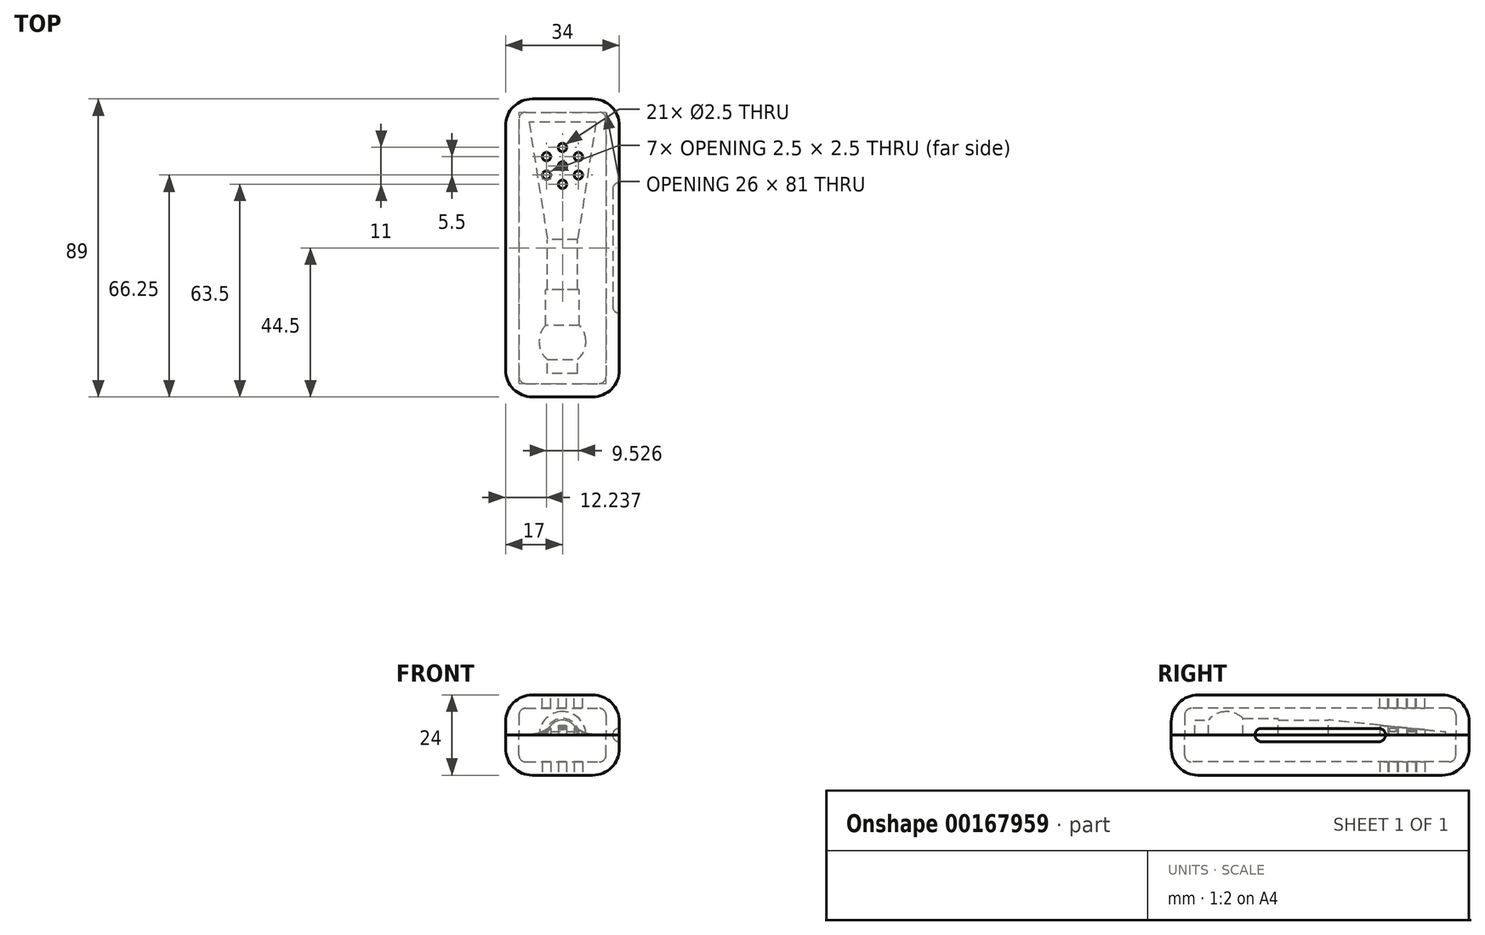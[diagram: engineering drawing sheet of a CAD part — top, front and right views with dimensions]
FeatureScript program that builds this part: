
annotation { "Feature Type Name" : "Feature", "Feature Type Description" : "" }
export const myFeature = defineFeature(function(context is Context, id is Id, definition is map)
    precondition{}
    {
        {
            var Q0;
            Q0=qCreatedBy(makeId("Front.planeOp"),FACE);
            cPlane(context, id + "F0", {"entities" : qUnion([Q0]), "cplaneType" : CPlaneType.OFFSET, "offset" : 35 * mm, "width" : 150 * mm, "height" : 150 * mm});
        }
        {
            var Q0;
            Q0=qCreatedBy(id+"F0.planeOp",FACE);
            var sketch = newSketch(context, id + "F1", { "sketchPlane" : qUnion([Q0])});
            skCircle(sketch, "E0", {"center": v(0, 0) * mm, "radius": 4.5 * mm});
            skSolve(sketch);
        }
        {
            var Q0;
            Q0=qCreatedBy(makeId("Front.planeOp"),FACE);
            var sketch = newSketch(context, id + "F2", { "sketchPlane" : qUnion([Q0])});
            skArc(sketch, "E1", {"start": v(10, 0) * mm, "mid": v(0, 1) * mm, "end": v(-10, 0) * mm});
            skLineSegment(sketch, "E2", {"start": v(-17.72, 1) * mm, "end": v(25.21, 1) * mm, "construction": true});
            skArc(sketch, "E3.MirrorCS", {"start": v(10, 0) * mm, "mid": v(0, -1) * mm, "end": v(-10, 0) * mm});
            skSolve(sketch);
        }
        {
            var Q0;
            Q0=makeQuery(id+"F1.imprint","IMPRINT",FACE,{"disambiguationData":[TD([[makeQuery(id+"F1.imprint","IMPRINT",EDGE,{"derivedFrom":sQuery(id+"F1.wireOp",EDGE,"E0")}),1.0]])]});
            extrude(context, id + "F3", {"entities" : qUnion([Q0]), "depth" : 40 * mm});
        }
        {
            var Q1;
            Q1=makeQuery(id+"F2.imprint","IMPRINT",FACE,{"disambiguationData":[TD([[makeQuery(id+"F2.imprint","IMPRINT",EDGE,{"derivedFrom":sQuery(id+"F2.wireOp",EDGE,"E1")}),1.0]])]});
            var Q2;
            Q2=makeQuery(id+"F1.imprint","IMPRINT",FACE,{"disambiguationData":[TD([[makeQuery(id+"F1.imprint","IMPRINT",EDGE,{"derivedFrom":sQuery(id+"F1.wireOp",EDGE,"E0")}),1.0]])]});
            loft(context, id + "F4", {"operationType" : NewBodyOperationType.ADD, "sheetProfilesArray" : [{ "sheetProfileEntities" : qUnion([Q1]) }, { "sheetProfileEntities" : qUnion([Q2]) }]});
        }
        {
            var Q0;
            Q0=makeQuery(id+"F3.opExtrude","CAP_FACE",FACE,{"disambiguationData":[OSD([sQuery(id+"F1.wireOp",EDGE,"E0")])],"isStart":false});
            cPlane(context, id + "F5", {"entities" : qUnion([Q0]), "cplaneType" : CPlaneType.OFFSET, "offset" : 9.5 * mm, "oppositeDirection" : true, "width" : 150 * mm, "height" : 150 * mm});
        }
        {
            var Q0;
            Q0=qCreatedBy(id+"F5.planeOp",FACE);
            var sketch = newSketch(context, id + "F6", { "sketchPlane" : qUnion([Q0])});
            skArc(sketch, "E4", {"start": v(0, 7) * mm, "mid": v(-7, 0) * mm, "end": v(0, -7) * mm});
            skLineSegment(sketch, "E5", {"start": v(0, 7) * mm, "end": v(0, -7) * mm});
            skSolve(sketch);
        }
        {
            var Q0;
            Q0=makeQuery(id+"F6.imprint","IMPRINT",FACE,{"disambiguationData":[TD([[makeQuery(id+"F6.imprint","IMPRINT",EDGE,{"derivedFrom":sQuery(id+"F6.wireOp",EDGE,"E4")}),1.0]])]});
            var Q1;
            Q1=sQuery(id+"F6.wireOp",EDGE,"E5");
            revolve(context, id + "F7", {"operationType" : NewBodyOperationType.ADD, "entities" : qUnion([Q0]), "axis" : qUnion([Q1]), "revolveType" : RevolveType.FULL});
        }
        {
            var Q0;
            Q0=makeQuery(id+"F3.opExtrude","CAP_FACE",FACE,{"disambiguationData":[OSD([sQuery(id+"F1.wireOp",EDGE,"E0")])],"isStart":false});
            cPlane(context, id + "F8", {"entities" : qUnion([Q0]), "cplaneType" : CPlaneType.OFFSET, "offset" : 25 * mm, "oppositeDirection" : true, "width" : 150 * mm, "height" : 150 * mm});
        }
        {
            var Q0;
            Q0=qCreatedBy(id+"F8.planeOp",FACE);
            var sketch = newSketch(context, id + "F9", { "sketchPlane" : qUnion([Q0])});
            skCircle(sketch, "E6", {"center": v(0, 0) * mm, "radius": 5 * mm});
            skSolve(sketch);
        }
        {
            var Q0;
            Q0=makeQuery(id+"F9.imprint","IMPRINT",FACE,{"disambiguationData":[TD([[makeQuery(id+"F9.imprint","IMPRINT",EDGE,{"derivedFrom":sQuery(id+"F9.wireOp",EDGE,"E6")}),1.0]])]});
            extrude(context, id + "F10", {"entities" : qUnion([Q0]), "operationType" : NewBodyOperationType.ADD, "endBound" : BoundingType.UP_TO_NEXT, "depth" : 25 * mm});
        }
        {
            assignVariable(context, id + "F11", {"name" : "wood", "anyValue" : 4 * mm});
        }
        {
            assignVariable(context, id + "F12", {"name" : "inner_corner", "anyValue" : 2 * mm});
        }
        {
            assignVariable(context, id + "F13", {"name" : "outer_corner", "anyValue" : 8 * mm});
        }
        {
            assignVariable(context, id + "F14", {"name" : "box_thickness", "anyValue" : 12 * mm});
        }
        {
            var Q0;
            Q0=qCreatedBy(makeId("Top.planeOp"),FACE);
            var sketch = newSketch(context, id + "F15", { "sketchPlane" : qUnion([Q0])});
            skLineSegment(sketch, "E7", {"start": v(31.86, 0) * mm, "end": v(31.86, -37.5) * mm, "construction": true});
            skLineSegment(sketch, "E8", {"start": v(31.86, -37.5) * mm, "end": v(31.86, -75) * mm, "construction": true});
            skLineSegment(sketch, "E9", {"start": v(0, 0) * mm, "end": v(31.86, 0) * mm, "construction": true});
            skLineSegment(sketch, "E10", {"start": v(31.86, -75) * mm, "end": v(-31.65, -75) * mm, "construction": true});
            skLineSegment(sketch, "E11.bottom", {"start": v(17, -82) * mm, "end": v(-17, -82) * mm});
            skLineSegment(sketch, "E11.top", {"start": v(17, 7) * mm, "end": v(-17, 7) * mm});
            skLineSegment(sketch, "E11.left", {"start": v(17, -82) * mm, "end": v(17, 7) * mm});
            skLineSegment(sketch, "E11.right", {"start": v(-17, -82) * mm, "end": v(-17, 7) * mm});
            skPoint(sketch, "E11.middle", {"position": v(0, -37.5) * mm});
            skLineSegment(sketch, "E12", {"start": v(31.86, -37.5) * mm, "end": v(-50.29, -37.5) * mm, "construction": true});
            skPoint(sketch, "E13", {"position": v(-9.21, -37.5) * mm});
            skSolve(sketch);
        }
        {
            var Q0;
            Q0=makeQuery(id+"F15.imprint","IMPRINT",FACE,{"disambiguationData":[TD([[makeQuery(id+"F15.imprint","IMPRINT",EDGE,{"derivedFrom":sQuery(id+"F15.wireOp",EDGE,"E11.bottom")}),-1.0]])]});
            extrude(context, id + "F16", {"entities" : qUnion([Q0]), "oppositeDirection" : true, "depth" : getVariable(context, 'box_thickness')});
        }
        {
            var Q0;
            Q0=makeQuery(id+"F16.opExtrude","CAP_FACE",FACE,{"disambiguationData":[OSD([sQuery(id+"F15.wireOp",EDGE,"E11.bottom"),sQuery(id+"F15.wireOp",EDGE,"E11.top"),sQuery(id+"F15.wireOp",EDGE,"E11.left"),sQuery(id+"F15.wireOp",EDGE,"E11.right")])],"isStart":true});
            var sketch = newSketch(context, id + "F17", { "sketchPlane" : qUnion([Q0])});
            skLineSegment(sketch, "E14.bottom", {"start": v(-13, 3) * mm, "end": v(13, 3) * mm});
            skLineSegment(sketch, "E14.top", {"start": v(-13, -78) * mm, "end": v(13, -78) * mm});
            skLineSegment(sketch, "E14.left", {"start": v(-13, 3) * mm, "end": v(-13, -78) * mm});
            skLineSegment(sketch, "E14.right", {"start": v(13, 3) * mm, "end": v(13, -78) * mm});
            skPoint(sketch, "E15.visualSharp", {"position": v(-13, 3) * mm});
            skPoint(sketch, "E16.visualSharp", {"position": v(13, 3) * mm});
            skPoint(sketch, "E17.visualSharp", {"position": v(13, -78) * mm});
            skPoint(sketch, "E18.visualSharp", {"position": v(-13, -78) * mm});
            skSolve(sketch);
        }
        {
            var Q0;
            Q0=makeQuery(id+"F17.imprint","IMPRINT",FACE,{"disambiguationData":[TD([[makeQuery(id+"F17.imprint","IMPRINT",EDGE,{"derivedFrom":sQuery(id+"F17.wireOp",EDGE,"E14.bottom")}),-1.0]])]});
            extrude(context, id + "F18", {"entities" : qUnion([Q0]), "operationType" : NewBodyOperationType.REMOVE, "oppositeDirection" : true, "depth" : getVariable(context, 'box_thickness') - getVariable(context, 'wood')});
        }
        {
            var Q0;
            Q0=makeQuery(id+"F18.boolean.opBoolean","COPY",EDGE,{"derivedFrom":makeQuery(id+"F18.opExtrude","CAP_EDGE",EDGE,{"disambiguationData":[OSD([sQuery(id+"F17.wireOp",EDGE,"E14.bottom")])],"isStart":false})});
            var Q1;
            Q1=makeQuery(id+"F18.boolean.opBoolean","COPY",EDGE,{"derivedFrom":makeQuery(id+"F18.opExtrude","SWEPT_EDGE",EDGE,{"disambiguationData":[OSD([sQuery(id+"F17.wireOp",EDGE,"E14.bottom"),sQuery(id+"F17.wireOp",EDGE,"E14.right")])]})});
            var Q2;
            Q2=makeQuery(id+"F18.boolean.opBoolean","COPY",EDGE,{"derivedFrom":makeQuery(id+"F18.opExtrude","CAP_EDGE",EDGE,{"disambiguationData":[OSD([sQuery(id+"F17.wireOp",EDGE,"E14.right")])],"isStart":false})});
            var Q3;
            Q3=makeQuery(id+"F18.boolean.opBoolean","COPY",EDGE,{"derivedFrom":makeQuery(id+"F18.opExtrude","SWEPT_EDGE",EDGE,{"disambiguationData":[OSD([sQuery(id+"F17.wireOp",EDGE,"E14.bottom"),sQuery(id+"F17.wireOp",EDGE,"E14.left")])]})});
            var Q4;
            Q4=makeQuery(id+"F18.boolean.opBoolean","COPY",EDGE,{"derivedFrom":makeQuery(id+"F18.opExtrude","CAP_EDGE",EDGE,{"disambiguationData":[OSD([sQuery(id+"F17.wireOp",EDGE,"E14.left")])],"isStart":false})});
            var Q5;
            Q5=makeQuery(id+"F18.boolean.opBoolean","COPY",EDGE,{"derivedFrom":makeQuery(id+"F18.opExtrude","SWEPT_EDGE",EDGE,{"disambiguationData":[OSD([sQuery(id+"F17.wireOp",EDGE,"E14.top"),sQuery(id+"F17.wireOp",EDGE,"E14.right")])]})});
            var Q6;
            Q6=makeQuery(id+"F18.boolean.opBoolean","COPY",EDGE,{"derivedFrom":makeQuery(id+"F18.opExtrude","CAP_EDGE",EDGE,{"disambiguationData":[OSD([sQuery(id+"F17.wireOp",EDGE,"E14.top")])],"isStart":false})});
            var Q7;
            Q7=makeQuery(id+"F18.boolean.opBoolean","COPY",EDGE,{"derivedFrom":makeQuery(id+"F18.opExtrude","SWEPT_EDGE",EDGE,{"disambiguationData":[OSD([sQuery(id+"F17.wireOp",EDGE,"E14.top"),sQuery(id+"F17.wireOp",EDGE,"E14.left")])]})});
            fillet(context, id + "F19", {"entities" : qUnion([Q0, Q1, Q2, Q3, Q4, Q5, Q6, Q7]), "radius" : getVariable(context, 'inner_corner'), "tangentPropagation" : true, "allowEdgeOverflow" : false});
        }
        {
            var Q0;
            Q0=makeQuery(id+"F16.opExtrude","SWEPT_EDGE",EDGE,{"disambiguationData":[OSD([sQuery(id+"F15.wireOp",EDGE,"E11.top"),sQuery(id+"F15.wireOp",EDGE,"E11.left")])]});
            var Q1;
            Q1=makeQuery(id+"F16.opExtrude","CAP_EDGE",EDGE,{"disambiguationData":[OSD([sQuery(id+"F15.wireOp",EDGE,"E11.left")])],"isStart":false});
            var Q2;
            Q2=makeQuery(id+"F16.opExtrude","CAP_EDGE",EDGE,{"disambiguationData":[OSD([sQuery(id+"F15.wireOp",EDGE,"E11.top")])],"isStart":false});
            var Q3;
            Q3=makeQuery(id+"F16.opExtrude","CAP_EDGE",EDGE,{"disambiguationData":[OSD([sQuery(id+"F15.wireOp",EDGE,"E11.right")])],"isStart":false});
            var Q4;
            Q4=makeQuery(id+"F16.opExtrude","SWEPT_EDGE",EDGE,{"disambiguationData":[OSD([sQuery(id+"F15.wireOp",EDGE,"E11.top"),sQuery(id+"F15.wireOp",EDGE,"E11.right")])]});
            var Q5;
            Q5=makeQuery(id+"F16.opExtrude","SWEPT_EDGE",EDGE,{"disambiguationData":[OSD([sQuery(id+"F15.wireOp",EDGE,"E11.bottom"),sQuery(id+"F15.wireOp",EDGE,"E11.right")])]});
            var Q6;
            Q6=makeQuery(id+"F16.opExtrude","CAP_EDGE",EDGE,{"disambiguationData":[OSD([sQuery(id+"F15.wireOp",EDGE,"E11.bottom")])],"isStart":false});
            var Q7;
            Q7=makeQuery(id+"F16.opExtrude","SWEPT_EDGE",EDGE,{"disambiguationData":[OSD([sQuery(id+"F15.wireOp",EDGE,"E11.bottom"),sQuery(id+"F15.wireOp",EDGE,"E11.left")])]});
            fillet(context, id + "F20", {"entities" : qUnion([Q0, Q1, Q2, Q3, Q4, Q5, Q6, Q7]), "radius" : getVariable(context, 'outer_corner'), "tangentPropagation" : true, "allowEdgeOverflow" : false});
        }
        {
            var Q0;
            Q0=makeQuery(id+"F16.opExtrude","CAP_FACE",FACE,{"disambiguationData":[OSD([sQuery(id+"F15.wireOp",EDGE,"E11.bottom"),sQuery(id+"F15.wireOp",EDGE,"E11.top"),sQuery(id+"F15.wireOp",EDGE,"E11.left"),sQuery(id+"F15.wireOp",EDGE,"E11.right")])],"isStart":false});
            var sketch = newSketch(context, id + "F21", { "sketchPlane" : qUnion([Q0])});
            skCircle(sketch, "E19", {"center": v(0, 7.5) * mm, "radius": 1.25 * mm});
            skCircle(sketch, "E20", {"center": v(0, 13) * mm, "radius": 1.25 * mm});
            skCircle(sketch, "E21", {"center": v(0, 18.5) * mm, "radius": 1.25 * mm});
            skCircle(sketch, "E22", {"center": v(4.76, 15.75) * mm, "radius": 1.25 * mm});
            skCircle(sketch, "E23", {"center": v(4.76, 10.25) * mm, "radius": 1.25 * mm});
            skCircle(sketch, "E24", {"center": v(-4.76, 15.75) * mm, "radius": 1.25 * mm});
            skCircle(sketch, "E25", {"center": v(-4.76, 10.25) * mm, "radius": 1.25 * mm});
            skLineSegment(sketch, "E26", {"start": v(0, 18.5) * mm, "end": v(4.76, 15.75) * mm, "construction": true});
            skLineSegment(sketch, "E27", {"start": v(4.76, 15.75) * mm, "end": v(4.76, 10.25) * mm, "construction": true});
            skLineSegment(sketch, "E28", {"start": v(4.76, 10.25) * mm, "end": v(0, 13) * mm, "construction": true});
            skLineSegment(sketch, "E29", {"start": v(0, 7.5) * mm, "end": v(0, 13) * mm, "construction": true});
            skLineSegment(sketch, "E30", {"start": v(0, 13) * mm, "end": v(0, 18.5) * mm, "construction": true});
            skLineSegment(sketch, "E31", {"start": v(-4.76, 15.75) * mm, "end": v(0, 13) * mm, "construction": true});
            skLineSegment(sketch, "E32", {"start": v(-4.76, 15.75) * mm, "end": v(-4.76, 10.25) * mm, "construction": true});
            skLineSegment(sketch, "E33", {"start": v(-4.76, 10.25) * mm, "end": v(0, 7.5) * mm, "construction": true});
            skLineSegment(sketch, "E34", {"start": v(-4.76, 15.75) * mm, "end": v(0, 18.5) * mm, "construction": true});
            skLineSegment(sketch, "E35", {"start": v(4.76, 10.25) * mm, "end": v(0, 7.5) * mm, "construction": true});
            skSolve(sketch);
        }
        {
            var Q0;
            Q0=makeQuery(id+"F21.imprint","IMPRINT",FACE,{"disambiguationData":[TD([[makeQuery(id+"F21.imprint","IMPRINT",EDGE,{"derivedFrom":sQuery(id+"F21.wireOp",EDGE,"E22")}),1.0]])]});
            var Q1;
            Q1=makeQuery(id+"F21.imprint","IMPRINT",FACE,{"disambiguationData":[TD([[makeQuery(id+"F21.imprint","IMPRINT",EDGE,{"derivedFrom":sQuery(id+"F21.wireOp",EDGE,"E23")}),1.0]])]});
            var Q2;
            Q2=makeQuery(id+"F21.imprint","IMPRINT",FACE,{"disambiguationData":[TD([[makeQuery(id+"F21.imprint","IMPRINT",EDGE,{"derivedFrom":sQuery(id+"F21.wireOp",EDGE,"E19")}),1.0]])]});
            var Q3;
            Q3=makeQuery(id+"F21.imprint","IMPRINT",FACE,{"disambiguationData":[TD([[makeQuery(id+"F21.imprint","IMPRINT",EDGE,{"derivedFrom":sQuery(id+"F21.wireOp",EDGE,"E20")}),1.0]])]});
            var Q4;
            Q4=makeQuery(id+"F21.imprint","IMPRINT",FACE,{"disambiguationData":[TD([[makeQuery(id+"F21.imprint","IMPRINT",EDGE,{"derivedFrom":sQuery(id+"F21.wireOp",EDGE,"E21")}),1.0]])]});
            var Q5;
            Q5=makeQuery(id+"F21.imprint","IMPRINT",FACE,{"disambiguationData":[TD([[makeQuery(id+"F21.imprint","IMPRINT",EDGE,{"derivedFrom":sQuery(id+"F21.wireOp",EDGE,"E24")}),1.0]])]});
            var Q6;
            Q6=makeQuery(id+"F21.imprint","IMPRINT",FACE,{"disambiguationData":[TD([[makeQuery(id+"F21.imprint","IMPRINT",EDGE,{"derivedFrom":sQuery(id+"F21.wireOp",EDGE,"E25")}),1.0]])]});
            extrude(context, id + "F22", {"entities" : qUnion([Q0, Q1, Q2, Q3, Q4, Q5, Q6]), "operationType" : NewBodyOperationType.REMOVE, "oppositeDirection" : true, "depth" : 25 * mm});
        }
        {
            var Q0;
            Q0=makeQuery(id+"F16.opExtrude","CAP_FACE",FACE,{"disambiguationData":[OSD([sQuery(id+"F15.wireOp",EDGE,"E11.bottom"),sQuery(id+"F15.wireOp",EDGE,"E11.top"),sQuery(id+"F15.wireOp",EDGE,"E11.left"),sQuery(id+"F15.wireOp",EDGE,"E11.right")])],"isStart":true});
            var sketch = newSketch(context, id + "F23", { "sketchPlane" : qUnion([Q0])});
            skLineSegment(sketch, "E36.bottom", {"start": v(15, -18) * mm, "end": v(18, -18) * mm});
            skLineSegment(sketch, "E36.top", {"start": v(15, -57) * mm, "end": v(18, -57) * mm});
            skLineSegment(sketch, "E36.left", {"start": v(15, -18) * mm, "end": v(15, -57) * mm});
            skLineSegment(sketch, "E36.right", {"start": v(18, -18) * mm, "end": v(18, -57) * mm});
            skSolve(sketch);
        }
        {
            var Q0;
            {var subQ0=sQuery(id+"F23.wireOp",EDGE,"E36.left");Q0=makeQuery(id+"F23.imprint","IMPRINT",FACE,{"disambiguationData":[TD([[makeQuery(id+"F23.imprint","IMPRINT",EDGE,{"derivedFrom":subQ0}),1.0]])]});}
            extrude(context, id + "F24", {"entities" : qUnion([Q0]), "operationType" : NewBodyOperationType.REMOVE, "oppositeDirection" : true, "depth" : getVariable(context, 'wood') / 2});
        }
        {
            var Q0;
            Q0=makeQuery(id+"F24.boolean.opBoolean","COPY",EDGE,{"derivedFrom":makeQuery(id+"F24.opExtrude","CAP_EDGE",EDGE,{"disambiguationData":[OSD([sQuery(id+"F23.wireOp",EDGE,"E36.left")])],"isStart":false})});
            var Q1;
            Q1=makeQuery(id+"F24.boolean.opBoolean","COPY",EDGE,{"derivedFrom":makeQuery(id+"F24.opExtrude","SWEPT_EDGE",EDGE,{"disambiguationData":[OSD([sQuery(id+"F23.wireOp",EDGE,"E36.top"),sQuery(id+"F23.wireOp",EDGE,"E36.left")])]})});
            var Q2;
            Q2=makeQuery(id+"F24.boolean.opBoolean","COPY",EDGE,{"derivedFrom":makeQuery(id+"F24.opExtrude","CAP_EDGE",EDGE,{"disambiguationData":[OSD([sQuery(id+"F23.wireOp",EDGE,"E36.top")])],"isStart":false})});
            var Q3;
            Q3=makeQuery(id+"F24.boolean.opBoolean","COPY",EDGE,{"derivedFrom":makeQuery(id+"F24.opExtrude","SWEPT_EDGE",EDGE,{"disambiguationData":[OSD([sQuery(id+"F23.wireOp",EDGE,"E36.bottom"),sQuery(id+"F23.wireOp",EDGE,"E36.left")])]})});
            var Q4;
            Q4=makeQuery(id+"F24.boolean.opBoolean","COPY",EDGE,{"derivedFrom":makeQuery(id+"F24.opExtrude","CAP_EDGE",EDGE,{"disambiguationData":[OSD([sQuery(id+"F23.wireOp",EDGE,"E36.bottom")])],"isStart":false})});
            fillet(context, id + "F25", {"entities" : qUnion([Q0, Q1, Q2, Q3, Q4]), "radius" : 2 * mm, "tangentPropagation" : true, "allowEdgeOverflow" : false});
        }
        {
            var Q0;
            Q0=makeQuery(id+"F16.opExtrude","SWEPT_BODY",BODY,{"disambiguationData":[OSD([sQuery(id+"F15.wireOp",EDGE,"E11.bottom"),sQuery(id+"F15.wireOp",EDGE,"E11.top"),sQuery(id+"F15.wireOp",EDGE,"E11.left"),sQuery(id+"F15.wireOp",EDGE,"E11.right")])]});
            var Q1;
            Q1=qCreatedBy(makeId("Top.planeOp"),FACE);
            mirror(context, id + "F26", {"entities" : qUnion([Q0]), "mirrorPlane" : qUnion([Q1])});
        }
    });
